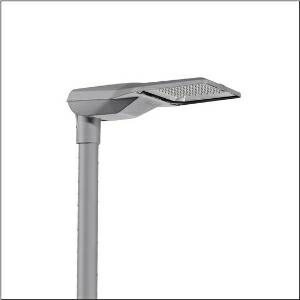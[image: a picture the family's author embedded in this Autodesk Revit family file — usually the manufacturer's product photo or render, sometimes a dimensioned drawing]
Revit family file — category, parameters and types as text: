
# Revit family: streetlight_sl_21_iq_midi___st1_5a_5xe3p41g08mb_0a3d
name_source: partatom
category: Lighting Fixtures
units: mm (PartAtom-declared; Revit-internal decimal feet)

## family parameters
Cut with Voids When Loaded = No
Host = Face
Light Source = No
Part Type = Normal
Room Calculation Point = No
Round Connector Dimension = Use Diameter
Shared = No

## types (1)
- --- (1 x LED, 20000 lm, 146.7 W, 4000K)
    Apparent Load = 147 VA
    CIE Flux Codes = 22 53 95 100 100
    Color Rendering = 70
    Color Temperature = 4000K
    Default Elevation = 1800 mm
    Description = Streetlight SL 21 iQ midi, mast luminaire, primary light control with lens, of PMMA, primary optical cover: cover, of toughened safety glass, transparent, light distribution: ST1.5a, light emission: direct distribution, primary light characteristic: asymmetric, installation type: post-top, side-entry, LED, High Power LED, rated luminous flux: 20.000lm, luminous efficacy: 136lm/W, light colour: 740, colour temperature: 4000K, control gear: iQ Street-Remote, control: Street-Remote, Auto-Match, Temp-Guard, Lumen-Switch, Night-Set, Smart-Wire, Light-Fading, Desk-Remote (wireless, voltage-free reading and setting of iQ features in the workshop via application-optimized NFC function/RFID function), optimised constant luminous flux control (CLO 2.0), pre-setting: linear dimming characteristic, mains connection: 230..240V, AC, 50/60Hz, start of lifetime: 147W, end of service life: 161W, reduction: 62W, luminaire housing, of diecast aluminium, powder-coated, Siteco® metallic grey (DB 702S), corrosivity category C5 mid according to DIN EN ISO 12944, please order mast flange separately, inclination adjustable: 0°, 5°, 10°, 15°, sealing non-destructively replaceable, multi-level sealing system, length: 644mm, width: 335mm, height: 110mm, mast flange for spigot size: 42mm (side-entry): 5XC10008XM4, 60/48mm (side-entry/post-top): 5XC10108XM2, 76/60mm (side-entry/post-top): 5XC10108XM1, mounting height: 4..8m, protection rating (complete): IP66, insulation class (complete): insulation class II (safety insulation), certification: CE, ENEC, ENEC+, VDE, impact resistance: IK10, permissible operating ambient temperature for outdoor applications: -40..+50°C, standard-compliant lighting for roads and squares, packaging unit: 1 piece

Light Distribution: ST1.5a
    Height = 111 mm
    Lamp = 1 x LED
    Lamp Light Flux = 20000 lm
    Lamp Power = 146.7 W
    Lamp count = 1
    Length = 644 mm
    Luminous efficacy = 136 lm/W
    Manufacturer = Siteco
    ModVariant = No
    Model = 5XE3P41G08MB
    Number of Poles = 1
    OnlyDefault = Yes
    Power Factor = 1
    Product Name = Streetlight SL 21 iQ midi | ST1.5a
    Product group = mast luminaire | pylon top
    ProductGroupID = 6100
    Protection Class = Protection class II
    Protection Degree = IP 66
    RLX_Detail_Level = 1
    RLX_Emergency_Light_Flux = 0 lm
    RLX_Emergency_Type = 0
    RLX_Emergency_Type_DB = No
    RlxData = <blob elided: 30429 chars, md5=571be764>
    Socket = socket
    Standby Power = 0 W
    System Light Flux = 20000 lm
    System Power = 147 W
    Type Comments = factory setting: luminous flux: 100 % | dim-lin: 254 | 753 mA
    Type Image = l_1004298.jpg
    URL = http://relux.com
    VarID = @adj_197685
    Voltage = 0 V
    Weight = 0.00 kg
    Width = 336 mm

## geometry (parser evidence)
native form markers: Blend x4, Sweep x11
no freeform markers — native parametric forms only
